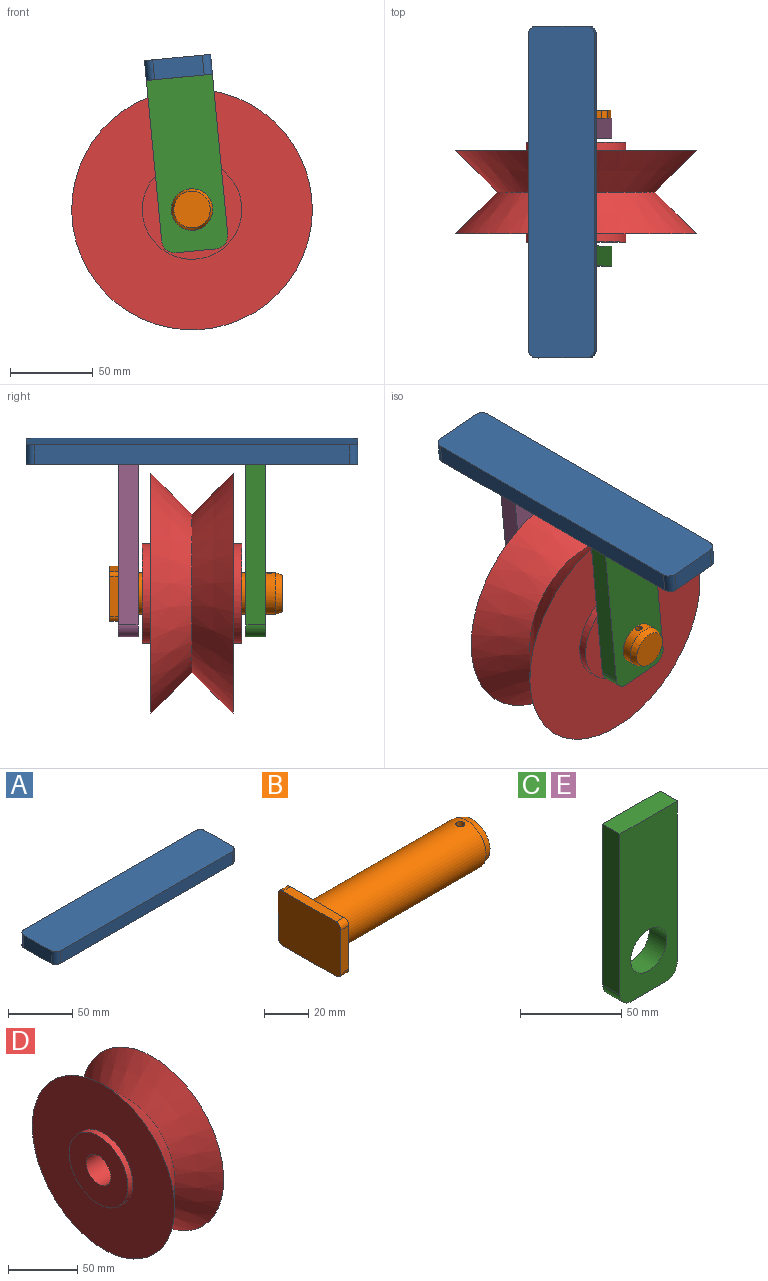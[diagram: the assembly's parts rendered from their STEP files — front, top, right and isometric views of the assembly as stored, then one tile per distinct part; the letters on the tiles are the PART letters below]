
ASSEMBLY  parts=5 mates=4
PART A: 10 faces, bbox 200x40x12 mm
  f0: plane 190x12mm, normal (0,1,0), area 2280mm2, adj f1,f7,f8,f9
  f1: cylinder r=5mm len=12mm, axis (0,0,-1), area 94.2mm2, adj f0,f2,f8,f9
  f2: plane 30x12mm, normal (-1,0,0), area 360mm2, adj f1,f3,f8,f9
  f3: cylinder r=5mm len=12mm, axis (0,0,-1), area 94.2mm2, adj f2,f4,f8,f9
  f4: plane 190x12mm, normal (0,-1,0), area 2280mm2, adj f3,f5,f8,f9
  f5: cylinder r=5mm len=12mm, axis (0,0,-1), area 94.2mm2, adj f4,f6,f8,f9
  f6: plane 30x12mm, normal (1,0,0), area 360mm2, adj f5,f7,f8,f9
  f7: cylinder r=5mm len=12mm, axis (0,0,-1), area 94.2mm2, adj f0,f6,f8,f9
  f8: plane 200x40mm, normal (0,0,1), area 7978.5mm2, adj f0,f1,f2,f3,f4,f5,f6,f7
  f9: plane 200x40mm, normal (0,0,-1), area 7978.5mm2, adj f0,f1,f2,f3,f4,f5,f6,f7
PART B: 14 faces, bbox 104x40x30 mm
  f0: cylinder r=12.5mm len=95mm, axis (-1,0,0), area 7436.1mm2, adj f2,f12,f13
  f1: plane 22x22mm, normal (1,0,0), area 380.1mm2, adj f2
  f2: cone r=11mm half-angle=20.6deg, axis (-1,0,0), area 315.4mm2, adj f0,f1
  f3: plane 24x5mm, normal (0,-1,0), area 120mm2, adj f4,f10,f11,f12
  f4: cylinder r=3mm len=5mm, axis (1,0,0), area 23.6mm2, adj f3,f5,f11,f12
  f5: plane 34x5mm, normal (0,0,1), area 170mm2, adj f4,f6,f11,f12
  f6: cylinder r=3mm len=5mm, axis (1,0,0), area 23.6mm2, adj f5,f7,f11,f12
  f7: plane 24x5mm, normal (0,1,0), area 120mm2, adj f6,f8,f11,f12
  f8: cylinder r=3mm len=5mm, axis (1,0,0), area 23.6mm2, adj f7,f9,f11,f12
  f9: plane 34x5mm, normal (0,0,-1), area 170mm2, adj f8,f10,f11,f12
  f10: cylinder r=3mm len=5mm, axis (1,0,0), area 23.6mm2, adj f3,f9,f11,f12
  f11: plane 40x30mm, normal (-1,0,0), area 1192.3mm2, adj f3,f4,f5,f6,f7,f8,f9,f10
  f12: plane 40x30mm, normal (1,0,0), area 701.4mm2, adj f0,f3,f4,f5,f6,f7,f8,f9
  f13: cylinder r=2mm len=25mm, axis (0,0,1), area 312.1mm2, adj f0
PART C: 9 faces, bbox 40x12x105 mm
  f0: plane 97x12mm, normal (-1,0,0), area 1164mm2, adj f1,f5,f7,f8
  f1: cylinder r=8mm len=12mm, axis (0,1,0), area 150.8mm2, adj f0,f2,f7,f8
  f2: plane 24x12mm, normal (0,0,-1), area 288mm2, adj f1,f3,f7,f8
  f3: cylinder r=8mm len=12mm, axis (0,1,0), area 150.8mm2, adj f2,f4,f7,f8
  f4: plane 97x12mm, normal (1,0,0), area 1164mm2, adj f3,f5,f7,f8
  f5: plane 40x12mm, normal (0,0,1), area 480mm2, adj f0,f4,f7,f8
  f6: cylinder r=12.5mm len=25mm, axis (0,1,0), area 942.5mm2, adj f7,f8
  f7: plane 105x40mm, normal (0,-1,0), area 3681.7mm2, adj f0,f1,f2,f3,f4,f5,f6
  f8: plane 105x40mm, normal (0,1,0), area 3681.7mm2, adj f0,f1,f2,f3,f4,f5,f6
PART D: 18 faces, bbox 60x145x145 mm
  f0: plane 145x145mm, normal (1,0,0), area 13539.6mm2, adj f2,f3,f9,f10,f11,f12,f13,f14
  f1: plane 60x60mm, normal (1,0,0), area 2336.6mm2, adj f2,f8
  f2: cylinder r=30mm len=60mm, axis (-1,0,0), area 942.5mm2, adj f0,f1
  f3: cone r=47.5mm half-angle=45deg, axis (1,0,0), area 13328.6mm2, adj f0,f4
  f4: cone r=72.5mm half-angle=45deg, axis (-1,0,0), area 13328.6mm2, adj f3,f5
  f5: plane 145x145mm, normal (-1,0,0), area 13685.6mm2, adj f4,f6
  f6: cylinder r=30mm len=60mm, axis (-1,0,0), area 942.5mm2, adj f5,f7
  f7: plane 60x60mm, normal (-1,0,0), area 2336.6mm2, adj f6,f8
  f8: cylinder r=12.5mm len=60mm, axis (-1,0,0), area 4712.4mm2, adj f1,f7
  f9: plane 16x2mm, normal (0,0,-1), area 32mm2, adj f0,f10,f16,f17
  f10: plane 5x2mm, normal (0,1,0), area 10mm2, adj f0,f9,f11,f17
  f11: plane 5x2mm, normal (0,0,1), area 10mm2, adj f0,f10,f12,f17
  f12: plane 11x2mm, normal (0,1,0), area 22mm2, adj f0,f11,f13,f17
  f13: plane 6x2mm, normal (0,0,1), area 12mm2, adj f0,f12,f14,f17
  f14: plane 11x2mm, normal (0,-1,0), area 22mm2, adj f0,f13,f15,f17
  f15: plane 5x2mm, normal (0,0,1), area 10mm2, adj f0,f14,f16,f17
  f16: plane 5x2mm, normal (0,-1,0), area 10mm2, adj f0,f9,f15,f17
  f17: plane 16x16mm, normal (1,0,0), area 146mm2, adj f9,f10,f11,f12,f13,f14,f15,f16
PART E: same geometry as C
PLACE A rot(axis=(-0.05,-0.05,1),90.1deg) t=(298.27,-189.7,-26.03)mm fixed
PLACE B rot(axis=(0.05,-0.05,-1),90.1deg) t=(473.39,-145.2,-89.67)mm
PLACE C rot(axis=(0,-1,0),5.5deg) t=(-106.42,-222.2,-131.8)mm
PLACE D rot(axis=(-0.43,-0.43,0.8),102.9deg) t=(309.32,213.11,-107.96)mm
PLACE E rot(axis=(0,-1,0),5.5deg) t=(-106.42,-145.2,-131.8)mm
MATE revolute D.f4 <-> C.f6  axis (0,-1,0) through (305.88,-219.7,-105.67)mm
MATE fastened A.f9 <-> E.f5  axis (0.1,0,-1) through (298.27,-189.7,-26.03)mm
MATE fastened C.f5 <-> A.f9  axis (-0.1,0,1) through (298.27,-222.2,-26.03)mm
MATE slider B.f0 <-> E.f6  axis (0,1,0) through (305.88,-145.2,-105.67)mm
